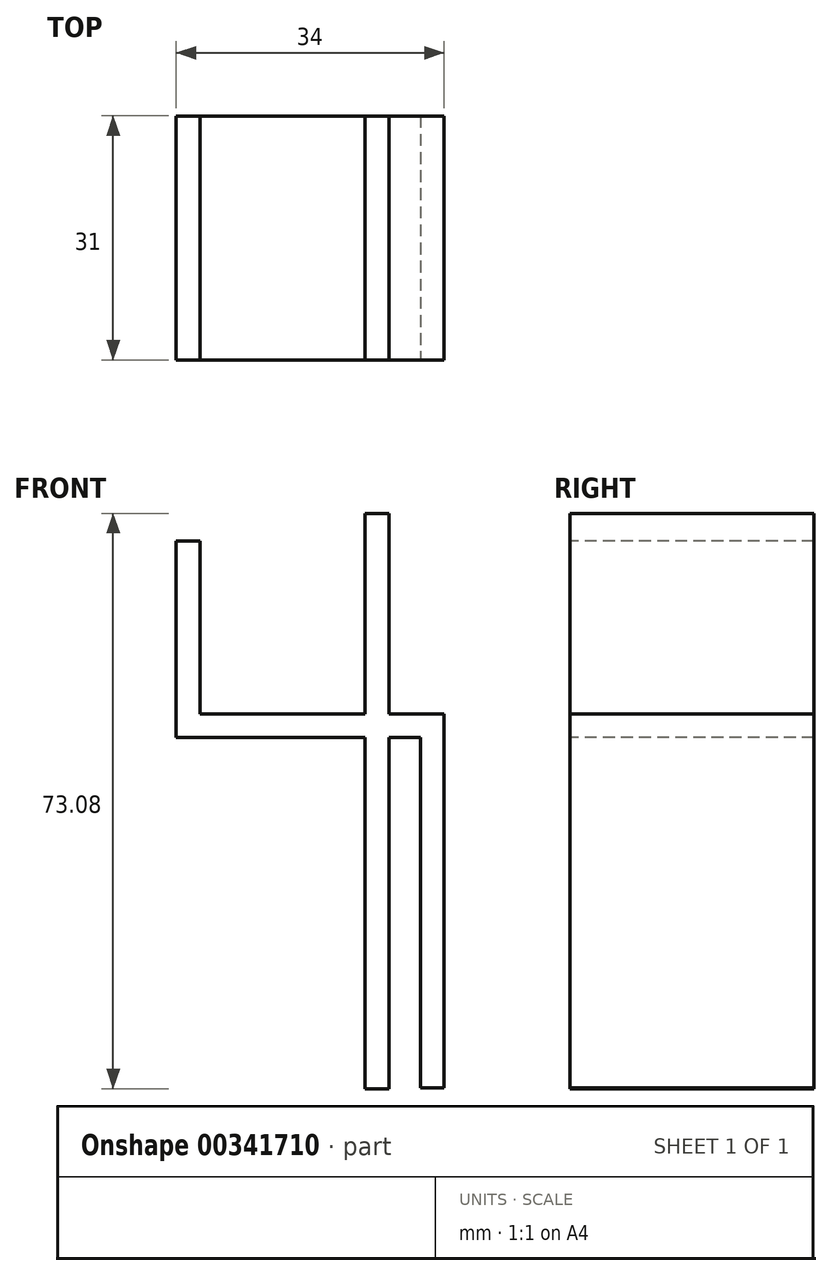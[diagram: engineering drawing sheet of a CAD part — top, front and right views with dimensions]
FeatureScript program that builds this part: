
annotation { "Feature Type Name" : "Feature", "Feature Type Description" : "" }
export const myFeature = defineFeature(function(context is Context, id is Id, definition is map)
    precondition{}
    {
        {
            var Q0;
            Q0=qCreatedBy(makeId("Top.planeOp"),FACE);
            var sketch = newSketch(context, id + "F0", { "sketchPlane" : qUnion([Q0])});
            skLineSegment(sketch, "E0.bottom", {"start": v(-14.15, 11.97) * mm, "end": v(-10.15, 11.97) * mm});
            skLineSegment(sketch, "E0.top", {"start": v(-14.15, -19.03) * mm, "end": v(-10.15, -19.03) * mm});
            skLineSegment(sketch, "E0.left", {"start": v(-14.15, 11.97) * mm, "end": v(-14.15, -19.03) * mm});
            skLineSegment(sketch, "E0.right", {"start": v(-10.15, 11.97) * mm, "end": v(-10.15, -19.03) * mm});
            skSolve(sketch);
        }
        {
            var Q0;
            Q0=makeQuery(id+"F0.imprint","IMPRINT",FACE,{"disambiguationData":[TD([[makeQuery(id+"F0.imprint","IMPRINT",EDGE,{"derivedFrom":sQuery(id+"F0.wireOp",EDGE,"E0.bottom")}),-1.0]])]});
            extrude(context, id + "F1", {"entities" : qUnion([Q0]), "depth" : 3 * mm});
        }
        {
            var Q0;
            Q0=makeQuery(id+"F1.opExtrude","SWEPT_FACE",FACE,{"disambiguationData":[OSD([sQuery(id+"F0.wireOp",EDGE,"E0.right")])]});
            var sketch = newSketch(context, id + "F2", { "sketchPlane" : qUnion([Q0])});
            skLineSegment(sketch, "E1.bottom", {"start": v(11.97, 3) * mm, "end": v(-19.03, 3) * mm});
            skLineSegment(sketch, "E1.top", {"start": v(11.97, -44.53) * mm, "end": v(-19.03, -44.53) * mm});
            skLineSegment(sketch, "E1.left", {"start": v(11.97, 3) * mm, "end": v(11.97, -44.53) * mm});
            skLineSegment(sketch, "E1.right", {"start": v(-19.03, 3) * mm, "end": v(-19.03, -44.53) * mm});
            skSolve(sketch);
        }
        {
            var Q0;
            Q0 = qSketchRegion(id + "F2", true);
            extrude(context, id + "F3", {"entities" : qUnion([Q0]), "operationType" : NewBodyOperationType.ADD, "depth" : 3 * mm});
        }
        {
            var Q0;
            Q0=makeQuery(id+"F1.opExtrude","SWEPT_FACE",FACE,{"disambiguationData":[OSD([sQuery(id+"F0.wireOp",EDGE,"E0.left")])]});
            var sketch = newSketch(context, id + "F4", { "sketchPlane" : qUnion([Q0])});
            skLineSegment(sketch, "E2.bottom", {"start": v(-11.97, 3) * mm, "end": v(19.03, 3) * mm});
            skLineSegment(sketch, "E2.top", {"start": v(-11.97, -44.6) * mm, "end": v(19.03, -44.6) * mm});
            skLineSegment(sketch, "E2.left", {"start": v(-11.97, 3) * mm, "end": v(-11.97, -44.6) * mm});
            skLineSegment(sketch, "E2.right", {"start": v(19.03, 3) * mm, "end": v(19.03, -44.6) * mm});
            skSolve(sketch);
        }
        {
            var Q0;
            {var subQ0=sQuery(id+"F4.wireOp",EDGE,"E2.top");Q0=makeQuery(id+"F4.imprint","IMPRINT",FACE,{"disambiguationData":[TD([[makeQuery(id+"F4.imprint","IMPRINT",EDGE,{"derivedFrom":subQ0}),1.0]])]});}
            extrude(context, id + "F5", {"entities" : qUnion([Q0]), "operationType" : NewBodyOperationType.ADD, "depth" : 3 * mm});
        }
        {
            var Q0;
            Q0=makeQuery(id+"F3.boolean.opBoolean","MERGE",FACE,{"derivedFrom":[makeQuery(id+"F1.opExtrude","CAP_FACE",FACE,{"disambiguationData":[OSD([sQuery(id+"F0.wireOp",EDGE,"E0.bottom"),sQuery(id+"F0.wireOp",EDGE,"E0.top"),sQuery(id+"F0.wireOp",EDGE,"E0.left"),sQuery(id+"F0.wireOp",EDGE,"E0.right")])],"isStart":false}),makeQuery(id+"F3.opExtrude","SWEPT_FACE",FACE,{"disambiguationData":[OSD([sQuery(id+"F2.wireOp",EDGE,"E1.bottom")])]})]});
            var sketch = newSketch(context, id + "F6", { "sketchPlane" : qUnion([Q0])});
            skLineSegment(sketch, "E3.bottom", {"start": v(-14.15, 11.97) * mm, "end": v(-38.15, 11.97) * mm});
            skLineSegment(sketch, "E3.top", {"start": v(-14.15, -19.03) * mm, "end": v(-38.15, -19.03) * mm});
            skLineSegment(sketch, "E3.left", {"start": v(-14.15, 11.97) * mm, "end": v(-14.15, -19.03) * mm});
            skLineSegment(sketch, "E3.right", {"start": v(-38.15, 11.97) * mm, "end": v(-38.15, -19.03) * mm});
            skSolve(sketch);
        }
        {
            var Q0;
            Q0 = qSketchRegion(id + "F6", true);
            var Q1;
            Q1=makeQuery(id+"F6.imprint","IMPRINT",FACE,{"disambiguationData":[TD([[makeQuery(id+"F6.imprint","IMPRINT",EDGE,{"derivedFrom":sQuery(id+"F6.wireOp",EDGE,"E3.bottom")}),1.0]])]});
            extrude(context, id + "F7", {"entities" : qUnion([Q0, Q1]), "operationType" : NewBodyOperationType.ADD, "depth" : -3 * mm});
        }
        {
            var Q0;
            Q0=makeQuery(id+"F7.opExtrude","CAP_FACE",FACE,{"disambiguationData":[OSD([sQuery(id+"F6.wireOp",EDGE,"E3.bottom"),sQuery(id+"F6.wireOp",EDGE,"E3.top"),sQuery(id+"F6.wireOp",EDGE,"E3.left"),sQuery(id+"F6.wireOp",EDGE,"E3.right")])],"isStart":false});
            var sketch = newSketch(context, id + "F8", { "sketchPlane" : qUnion([Q0])});
            skLineSegment(sketch, "E4.bottom", {"start": v(-41.15, -11.97) * mm, "end": v(-38.15, -11.97) * mm});
            skLineSegment(sketch, "E4.top", {"start": v(-41.15, 19.03) * mm, "end": v(-38.15, 19.03) * mm});
            skLineSegment(sketch, "E4.left", {"start": v(-38.15, 19.03) * mm, "end": v(-38.15, -11.97) * mm});
            skLineSegment(sketch, "E4.right", {"start": v(-41.15, 19.03) * mm, "end": v(-41.15, -11.97) * mm});
            skSolve(sketch);
        }
        {
            var Q0;
            Q0 = qSketchRegion(id + "F8", true);
            extrude(context, id + "F9", {"entities" : qUnion([Q0]), "operationType" : NewBodyOperationType.ADD, "depth" : -25 * mm});
        }
        {
            var Q0;
            Q0=makeQuery(id+"F5.opExtrude","CAP_FACE",FACE,{"disambiguationData":[OSD([sQuery(id+"F0.wireOp",EDGE,"E0.left"),sQuery(id+"F4.wireOp",EDGE,"E2.top"),sQuery(id+"F4.wireOp",EDGE,"E2.left"),sQuery(id+"F4.wireOp",EDGE,"E2.right")])],"isStart":false});
            var sketch = newSketch(context, id + "F10", { "sketchPlane" : qUnion([Q0])});
            skLineSegment(sketch, "E5.bottom", {"start": v(-11.97, 0) * mm, "end": v(19.03, 0) * mm});
            skLineSegment(sketch, "E5.top", {"start": v(-11.97, 28.48) * mm, "end": v(19.03, 28.48) * mm});
            skLineSegment(sketch, "E5.left", {"start": v(19.03, 0) * mm, "end": v(19.03, 28.48) * mm});
            skLineSegment(sketch, "E5.right", {"start": v(-11.97, 0) * mm, "end": v(-11.97, 28.48) * mm});
            skSolve(sketch);
        }
        {
            var Q0;
            Q0 = qSketchRegion(id + "F10", true);
            extrude(context, id + "F11", {"entities" : qUnion([Q0]), "operationType" : NewBodyOperationType.ADD, "depth" : -3 * mm});
        }
    });
